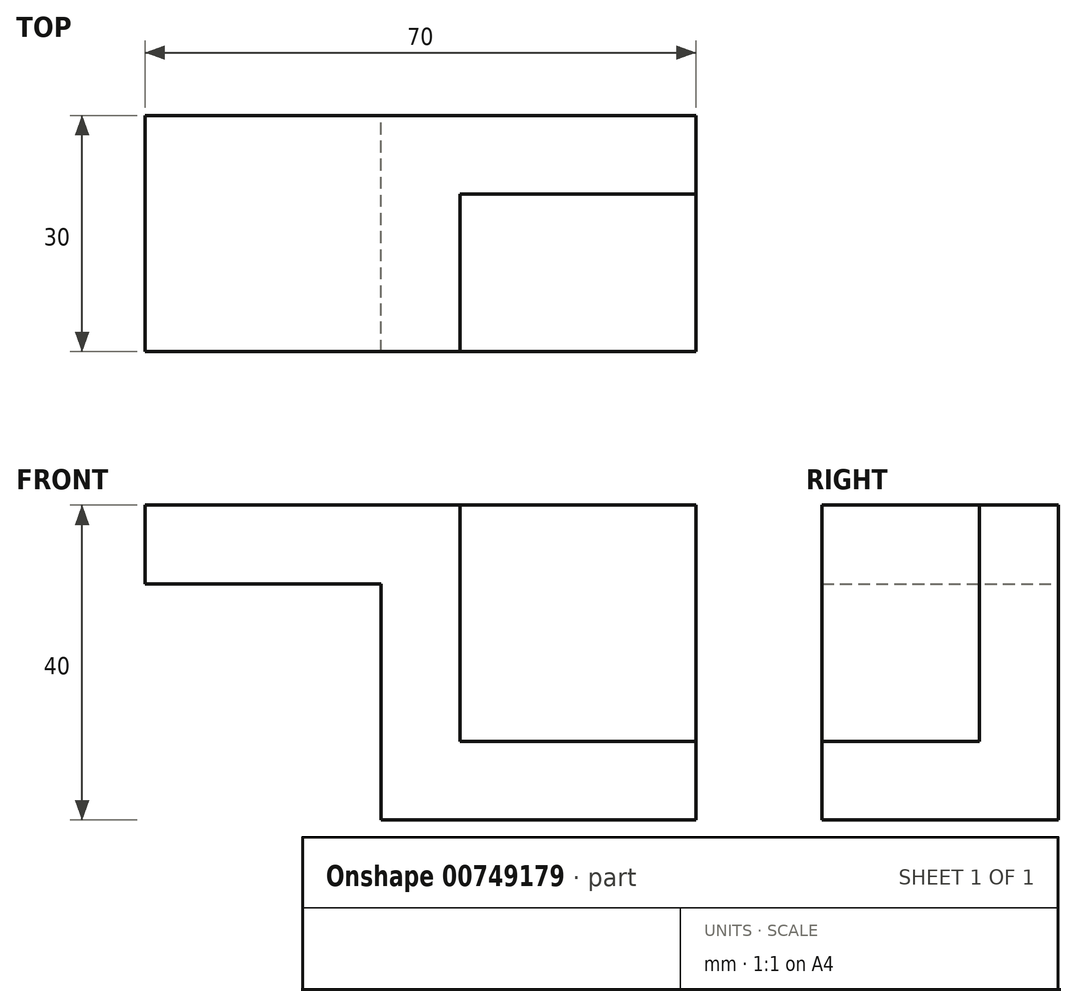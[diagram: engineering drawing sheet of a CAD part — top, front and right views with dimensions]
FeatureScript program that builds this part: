
annotation { "Feature Type Name" : "Feature", "Feature Type Description" : "" }
export const myFeature = defineFeature(function(context is Context, id is Id, definition is map)
    precondition{}
    {
        {
            var Q0;
            Q0=qCreatedBy(makeId("Front.planeOp"),FACE);
            var sketch = newSketch(context, id + "F0", { "sketchPlane" : qUnion([Q0])});
            skLineSegment(sketch, "E0", {"start": v(0, 0) * mm, "end": v(40, 0) * mm});
            skLineSegment(sketch, "E1", {"start": v(40, 0) * mm, "end": v(40, 10) * mm});
            skLineSegment(sketch, "E2", {"start": v(40, 10) * mm, "end": v(10, 10) * mm});
            skLineSegment(sketch, "E3", {"start": v(10, 10) * mm, "end": v(10, 40) * mm});
            skLineSegment(sketch, "E4", {"start": v(10, 40) * mm, "end": v(-30, 40) * mm});
            skLineSegment(sketch, "E5", {"start": v(-30, 40) * mm, "end": v(-30, 30) * mm});
            skLineSegment(sketch, "E6", {"start": v(-30, 30) * mm, "end": v(0, 30) * mm});
            skLineSegment(sketch, "E7", {"start": v(0, 30) * mm, "end": v(0, 0) * mm});
            skSolve(sketch);
        }
        {
            var Q0;
            Q0 = qSketchRegion(id + "F0", true);
            extrude(context, id + "F1", {"entities" : qUnion([Q0]), "depth" : 20 * mm, "offsetDistance" : 25 * mm});
        }
        {
            var Q0;
            Q0=makeQuery(id+"F1.opExtrude","CAP_FACE",FACE,{"disambiguationData":[OSD([sQuery(id+"F0.wireOp",EDGE,"E0"),sQuery(id+"F0.wireOp",EDGE,"E1"),sQuery(id+"F0.wireOp",EDGE,"E2"),sQuery(id+"F0.wireOp",EDGE,"E3"),sQuery(id+"F0.wireOp",EDGE,"E4"),sQuery(id+"F0.wireOp",EDGE,"E5"),sQuery(id+"F0.wireOp",EDGE,"E6"),sQuery(id+"F0.wireOp",EDGE,"E7")])],"isStart":true});
            var sketch = newSketch(context, id + "F2", { "sketchPlane" : qUnion([Q0])});
            skLineSegment(sketch, "E8", {"start": v(-40, 10) * mm, "end": v(-40, 0) * mm});
            skLineSegment(sketch, "E9", {"start": v(-40, 0) * mm, "end": v(0, 0) * mm});
            skLineSegment(sketch, "E10", {"start": v(0, 0) * mm, "end": v(0, 30) * mm});
            skLineSegment(sketch, "E11", {"start": v(0, 30) * mm, "end": v(30, 30) * mm});
            skLineSegment(sketch, "E12", {"start": v(30, 30) * mm, "end": v(30, 40) * mm});
            skLineSegment(sketch, "E13", {"start": v(30, 40) * mm, "end": v(-10, 40) * mm});
            skLineSegment(sketch, "E14", {"start": v(-10, 40) * mm, "end": v(-10, 10) * mm});
            skLineSegment(sketch, "E15", {"start": v(-10, 10) * mm, "end": v(-40, 10) * mm});
            skLineSegment(sketch, "E16", {"start": v(-40, 10) * mm, "end": v(-10, 10) * mm});
            skLineSegment(sketch, "E17", {"start": v(-10, 40) * mm, "end": v(-40, 40) * mm});
            skLineSegment(sketch, "E18", {"start": v(-40, 40) * mm, "end": v(-40, 10) * mm});
            skSolve(sketch);
        }
        {
            var Q0;
            Q0 = qSketchRegion(id + "F2", true);
            extrude(context, id + "F3", {"entities" : qUnion([Q0]), "operationType" : NewBodyOperationType.ADD, "depth" : 10 * mm, "offsetDistance" : 25 * mm});
        }
    });
